# Revit family: RN 84215 Optiflex-Flowpress-Gomito
name_source: partatom
category: Rohrzubehör
units: mm (PartAtom-declared; Revit-internal decimal feet)

## family parameters
Arbeitsebenenbasiert = Nein
Beim Laden mit Abzugskörper schneiden = Nein
Bemaßung runder Anschluss = Durchmesser verwenden
Gemeinsam genutzt = Nein
Immer vertikal = Ja
Teiletyp = Nicht definiert

## types (7) — shared parameters
1.010.00.2 Blattnummer der Richtlinie = 29
1.010.00.3 Ausgabedatum (Monat) der Richtlinie = 201308
1.010.00.4 Herstellername = R. Nussbaum AG
1.010.00.5 Revisionsdatum der Datei = 20190521
1.010.00.6 Webadresse des Herstellers = http://www.nussbaum.ch
1.100.00.4 Produktbezeichnung = Versorgung
1.110.00.2 Index = 5
1.110.00.4 Produktbezeichnung = Optiflex
1.960/3L.00.8 Link (URL) = https://www.nussbaum.ch
29.700.00.4 Produktname = Optiflex-Flowpress-Anschlusswinkel, mit Wandflansch
29.700.00.5 Produktkennung = 2
29.700.00.6 Querschnittsform = 1
29.700.00.7 Nennweitensystem = DN
29.700.00.8 Nenndrucksystem = PN
29.710.02.4 Nenndruck = 10
29.710.02.5 max. zul. Überdruck [hPa] = 1000
29.710.02.7 max. zul. Dauer-Betriebsdruck [hPa] = 1000
29.710.02.9 max. zul. Dauer-Betriebstemperatur [°C] = 70
Connector Visibility = Nein
EnclosingSpace Visibility = Nein
Hersteller = R. Nussbaum AG
URL = https://www.nussbaum.ch

## per-type parameters (varying)
- DN=2: 1.800.00.3 TGA-Nummer=01900500000000000000000000000000000000000000000007000000000000000007; 1.800.00.4 Kommentarfeld=84215.27, Optiflex-Flowpress-Anschlusswinkel, mit Wandflansch, DN=15, L=75, Rp=½; 1.810.00.3 Hersteller-Bestellnummer=84215.27; 1.810.00.4 DATANORM-Nummer=84215.27; 1.810.00.6 GTIN-Nummer=7612945730381; 29.710.02.10 Formstück-Gewicht [kg]=0.239; 29.710.02.3 Benennung=Optiflex-Flowpress-Anschlusswinkel, mit Wandflansch, DN=15, L=75, Rp=½; CONNECTOR0_DIAMETER_dZ_0r=15 mm; CONNECTOR0_dZ_00=54 mm; CONNECTOR0_dZ_01=40 mm; CONNECTOR0_ref_dX=18 mm; CONNECTOR0_ref_dZ=40 mm; CONNECTOR1_DIAMETER_dX_0r=15 mm; CONNECTOR1_dX_00=62 mm; CONNECTOR1_dX_01=75 mm; CONNECTOR1_ref_dX=62 mm; Modell=84215.27; R. Nussbaum AG 84215.21 de Visibility=Nein; R. Nussbaum AG 84215.22 de Visibility=Nein; R. Nussbaum AG 84215.23 de Visibility=Nein; R. Nussbaum AG 84215.24 de Visibility=Nein; R. Nussbaum AG 84215.25 de Visibility=Nein; R. Nussbaum AG 84215.26 de Visibility=Nein; R. Nussbaum AG 84215.27 de Visibility=Ja; Typenkommentare=Optiflex-Flowpress-Gomito DN=15
- DN=12x1: 1.800.00.3 TGA-Nummer=01900500000000000000000000000000000000000000000007000000000000000006; 1.800.00.4 Kommentarfeld=84215.26, Optiflex-Flowpress-Anschlusswinkel, mit Wandflansch, DN=12x15, L=75, Rp=½; 1.810.00.3 Hersteller-Bestellnummer=84215.26; 1.810.00.4 DATANORM-Nummer=84215.26; 1.810.00.6 GTIN-Nummer=7612945730374; 29.710.02.10 Formstück-Gewicht [kg]=0.229; 29.710.02.3 Benennung=Optiflex-Flowpress-Anschlusswinkel, mit Wandflansch, DN=12x15, L=75, Rp=½; CONNECTOR0_DIAMETER_dZ_0r=12 mm  [stored 0.0393701 ft]; CONNECTOR0_dZ_00=54 mm; CONNECTOR0_dZ_01=40 mm; CONNECTOR0_ref_dX=18 mm; CONNECTOR0_ref_dZ=40 mm; CONNECTOR1_DIAMETER_dX_0r=15 mm; CONNECTOR1_dX_00=62 mm; CONNECTOR1_dX_01=75 mm; CONNECTOR1_ref_dX=62 mm; Modell=84215.26; R. Nussbaum AG 84215.21 de Visibility=Nein; R. Nussbaum AG 84215.22 de Visibility=Nein; R. Nussbaum AG 84215.23 de Visibility=Nein; R. Nussbaum AG 84215.24 de Visibility=Nein; R. Nussbaum AG 84215.25 de Visibility=Nein; R. Nussbaum AG 84215.26 de Visibility=Ja; R. Nussbaum AG 84215.27 de Visibility=Nein; Typenkommentare=Optiflex-Flowpress-Gomito DN=12x15
- DN=1: 1.800.00.3 TGA-Nummer=01900500000000000000000000000000000000000000000007000000000000000005; 1.800.00.4 Kommentarfeld=84215.25, Optiflex-Flowpress-Anschlusswinkel, mit Wandflansch, DN=15, L=63, Rp=½; 1.810.00.3 Hersteller-Bestellnummer=84215.25; 1.810.00.4 DATANORM-Nummer=84215.25; 1.810.00.5 StLB-Nummer=342.412; 1.810.00.6 GTIN-Nummer=7612945730367; 29.710.02.10 Formstück-Gewicht [kg]=0.217; 29.710.02.3 Benennung=Optiflex-Flowpress-Anschlusswinkel, mit Wandflansch, DN=15, L=63, Rp=½; CONNECTOR0_DIAMETER_dZ_0r=15 mm; CONNECTOR0_dZ_00=54 mm; CONNECTOR0_dZ_01=40 mm; CONNECTOR0_ref_dX=18 mm; CONNECTOR0_ref_dZ=40 mm; CONNECTOR1_DIAMETER_dX_0r=15 mm; CONNECTOR1_dX_00=50 mm  [stored 0.164042 ft]; CONNECTOR1_dX_01=63 mm; CONNECTOR1_ref_dX=50 mm  [stored 0.164042 ft]; Modell=84215.25; R. Nussbaum AG 84215.21 de Visibility=Nein; R. Nussbaum AG 84215.22 de Visibility=Nein; R. Nussbaum AG 84215.23 de Visibility=Nein; R. Nussbaum AG 84215.24 de Visibility=Nein; R. Nussbaum AG 84215.25 de Visibility=Ja; R. Nussbaum AG 84215.26 de Visibility=Nein; R. Nussbaum AG 84215.27 de Visibility=Nein; Typenkommentare=Optiflex-Flowpress-Gomito DN=15
- DN=12x2: 1.800.00.3 TGA-Nummer=01900500000000000000000000000000000000000000000007000000000000000004; 1.800.00.4 Kommentarfeld=84215.24, Optiflex-Flowpress-Anschlusswinkel, mit Wandflansch, DN=12x15, L=63, Rp=½; 1.810.00.3 Hersteller-Bestellnummer=84215.24; 1.810.00.4 DATANORM-Nummer=84215.24; 1.810.00.5 StLB-Nummer=342.412; 1.810.00.6 GTIN-Nummer=7612945730350; 29.710.02.10 Formstück-Gewicht [kg]=0.19; 29.710.02.3 Benennung=Optiflex-Flowpress-Anschlusswinkel, mit Wandflansch, DN=12x15, L=63, Rp=½; CONNECTOR0_DIAMETER_dZ_0r=12 mm  [stored 0.0393701 ft]; CONNECTOR0_dZ_00=54 mm; CONNECTOR0_dZ_01=40 mm; CONNECTOR0_ref_dX=18 mm; CONNECTOR0_ref_dZ=40 mm; CONNECTOR1_DIAMETER_dX_0r=15 mm; CONNECTOR1_dX_00=50 mm  [stored 0.164042 ft]; CONNECTOR1_dX_01=63 mm; CONNECTOR1_ref_dX=50 mm  [stored 0.164042 ft]; Modell=84215.24; R. Nussbaum AG 84215.21 de Visibility=Nein; R. Nussbaum AG 84215.22 de Visibility=Nein; R. Nussbaum AG 84215.23 de Visibility=Nein; R. Nussbaum AG 84215.24 de Visibility=Ja; R. Nussbaum AG 84215.25 de Visibility=Nein; R. Nussbaum AG 84215.26 de Visibility=Nein; R. Nussbaum AG 84215.27 de Visibility=Nein; Typenkommentare=Optiflex-Flowpress-Gomito DN=12x15
- DN=3: 1.800.00.3 TGA-Nummer=01900500000000000000000000000000000000000000000007000000000000000003; 1.800.00.4 Kommentarfeld=84215.23, Optiflex-Flowpress-Anschlusswinkel, mit Wandflansch, DN=15, L=46, Rp=¾; 1.810.00.3 Hersteller-Bestellnummer=84215.23; 1.810.00.4 DATANORM-Nummer=84215.23; 1.810.00.5 StLB-Nummer=342.422; 1.810.00.6 GTIN-Nummer=7612945730466; 29.710.02.10 Formstück-Gewicht [kg]=0.17; 29.710.02.3 Benennung=Optiflex-Flowpress-Anschlusswinkel, mit Wandflansch, DN=15, L=46, Rp=¾; CONNECTOR0_DIAMETER_dZ_0r=15 mm; CONNECTOR0_dZ_00=53 mm; CONNECTOR0_dZ_01=39 mm; CONNECTOR0_ref_dX=17 mm; CONNECTOR0_ref_dZ=39 mm; CONNECTOR1_DIAMETER_dX_0r=20 mm; CONNECTOR1_dX_00=31 mm; CONNECTOR1_dX_01=46 mm; CONNECTOR1_ref_dX=31 mm; Modell=84215.23; R. Nussbaum AG 84215.21 de Visibility=Nein; R. Nussbaum AG 84215.22 de Visibility=Nein; R. Nussbaum AG 84215.23 de Visibility=Ja; R. Nussbaum AG 84215.24 de Visibility=Nein; R. Nussbaum AG 84215.25 de Visibility=Nein; R. Nussbaum AG 84215.26 de Visibility=Nein; R. Nussbaum AG 84215.27 de Visibility=Nein; Typenkommentare=Optiflex-Flowpress-Gomito DN=15
- DN=15: 1.800.00.3 TGA-Nummer=01900500000000000000000000000000000000000000000007000000000000000002; 1.800.00.4 Kommentarfeld=84215.22, Optiflex-Flowpress-Anschlusswinkel, mit Wandflansch, DN=15, L=45, Rp=½; 1.810.00.3 Hersteller-Bestellnummer=84215.22; 1.810.00.4 DATANORM-Nummer=84215.22; 1.810.00.5 StLB-Nummer=342.412; 1.810.00.6 GTIN-Nummer=7612945730459; 29.710.02.10 Formstück-Gewicht [kg]=0.127; 29.710.02.3 Benennung=Optiflex-Flowpress-Anschlusswinkel, mit Wandflansch, DN=15, L=45, Rp=½; CONNECTOR0_DIAMETER_dZ_0r=15 mm; CONNECTOR0_dZ_00=51 mm; CONNECTOR0_dZ_01=37 mm; CONNECTOR0_ref_dX=17 mm; CONNECTOR0_ref_dZ=37 mm; CONNECTOR1_DIAMETER_dX_0r=15 mm; CONNECTOR1_dX_00=32 mm  [stored 0.104987 ft]; CONNECTOR1_dX_01=45 mm; CONNECTOR1_ref_dX=32 mm  [stored 0.104987 ft]; Modell=84215.22; R. Nussbaum AG 84215.21 de Visibility=Nein; R. Nussbaum AG 84215.22 de Visibility=Ja; R. Nussbaum AG 84215.23 de Visibility=Nein; R. Nussbaum AG 84215.24 de Visibility=Nein; R. Nussbaum AG 84215.25 de Visibility=Nein; R. Nussbaum AG 84215.26 de Visibility=Nein; R. Nussbaum AG 84215.27 de Visibility=Nein; Typenkommentare=Optiflex-Flowpress-Gomito DN=15
- DN=12x15: 1.800.00.3 TGA-Nummer=01900500000000000000000000000000000000000000000007000000000000000001; 1.800.00.4 Kommentarfeld=84215.21, Optiflex-Flowpress-Anschlusswinkel, mit Wandflansch, DN=12x15, L=45, Rp=½; 1.810.00.3 Hersteller-Bestellnummer=84215.21; 1.810.00.4 DATANORM-Nummer=84215.21; 1.810.00.5 StLB-Nummer=342.411; 1.810.00.6 GTIN-Nummer=7612945730442; 29.710.02.10 Formstück-Gewicht [kg]=0.114; 29.710.02.3 Benennung=Optiflex-Flowpress-Anschlusswinkel, mit Wandflansch, DN=12x15, L=45, Rp=½; CONNECTOR0_DIAMETER_dZ_0r=12 mm  [stored 0.0393701 ft]; CONNECTOR0_dZ_00=51 mm; CONNECTOR0_dZ_01=37 mm; CONNECTOR0_ref_dX=17 mm; CONNECTOR0_ref_dZ=37 mm; CONNECTOR1_DIAMETER_dX_0r=15 mm; CONNECTOR1_dX_00=32 mm  [stored 0.104987 ft]; CONNECTOR1_dX_01=45 mm; CONNECTOR1_ref_dX=32 mm  [stored 0.104987 ft]; Modell=84215.21; R. Nussbaum AG 84215.21 de Visibility=Ja; R. Nussbaum AG 84215.22 de Visibility=Nein; R. Nussbaum AG 84215.23 de Visibility=Nein; R. Nussbaum AG 84215.24 de Visibility=Nein; R. Nussbaum AG 84215.25 de Visibility=Nein; R. Nussbaum AG 84215.26 de Visibility=Nein; R. Nussbaum AG 84215.27 de Visibility=Nein; Typenkommentare=Optiflex-Flowpress-Gomito DN=12x15

note: [stored X ft] marks values corroborated as IEEE doubles in the binary element streams (Revit-internal decimal feet)

## geometry (parser evidence)
native form markers: Sweep x1
no freeform markers — native parametric forms only
